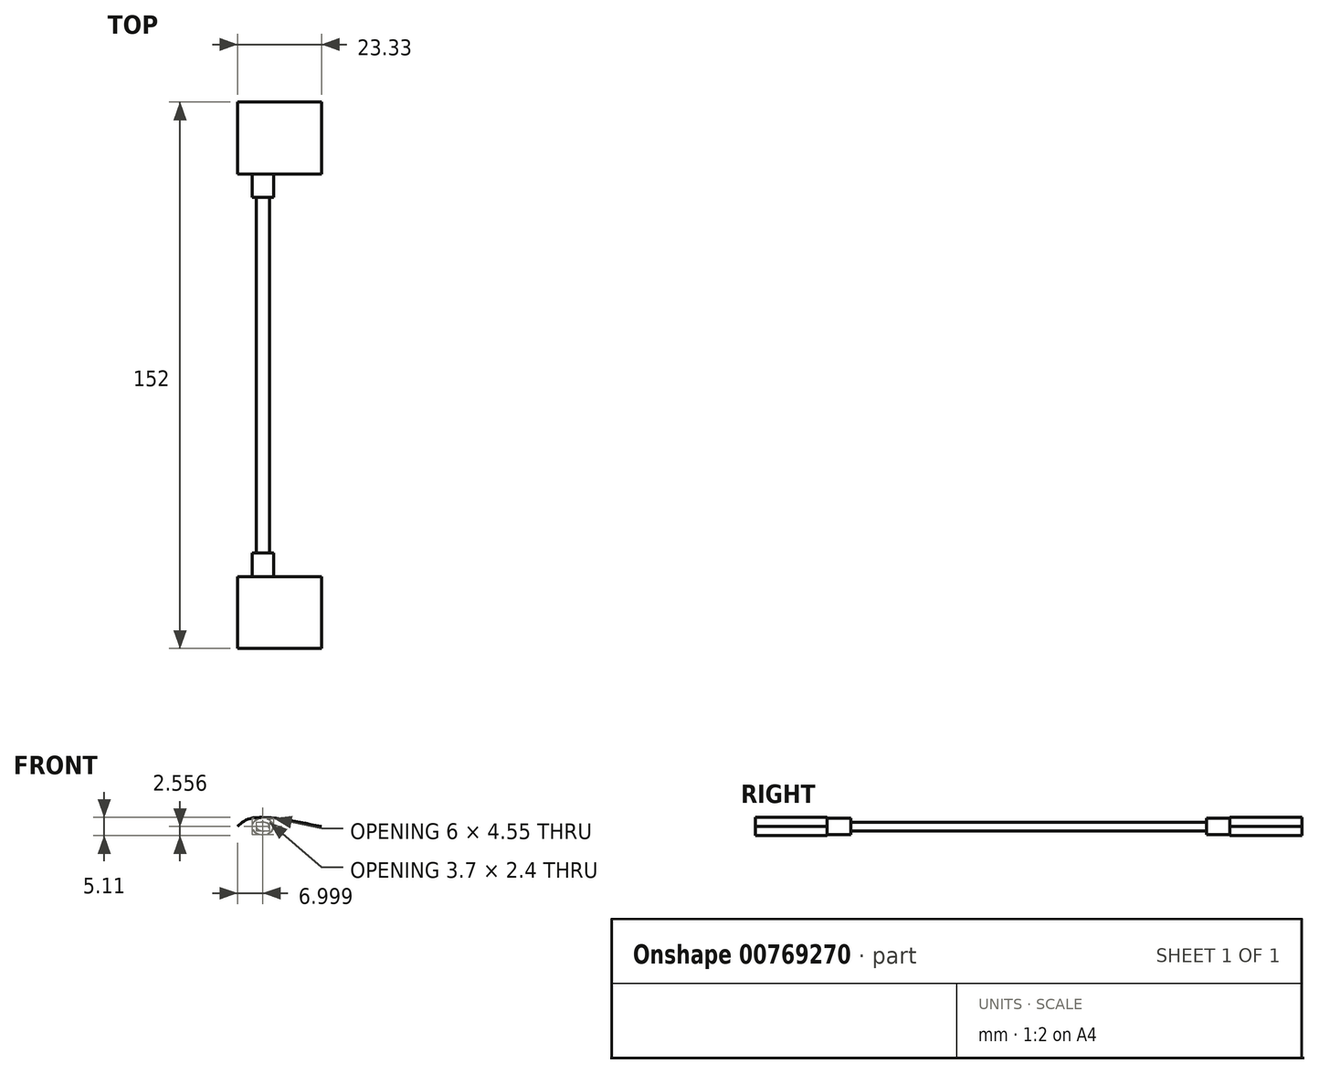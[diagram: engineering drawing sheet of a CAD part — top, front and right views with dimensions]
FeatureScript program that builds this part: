
annotation { "Feature Type Name" : "Feature", "Feature Type Description" : "" }
export const myFeature = defineFeature(function(context is Context, id is Id, definition is map)
    precondition{}
    {
        {
            var Q0;
            Q0=qCreatedBy(makeId("Front.planeOp"),FACE);
            var sketch = newSketch(context, id + "F0", { "sketchPlane" : qUnion([Q0])});
            skLineSegment(sketch, "E0", {"start": v(-22.8, 41.43) * mm, "end": v(4.53, 41.43) * mm, "construction": true});
            skPoint(sketch, "E0.startSnap0", {"position": v(-20.96, 41.43) * mm});
            skFitSpline(sketch, "E1", {"points": [v(-20.96, 41.43) * mm, v(-17.01, 43.75) * mm, v(2.37, 41.43) * mm], "startDerivative": vector(9.37, 8.85) * mm, "endDerivative": vector(34.4, -7.01) * mm});
            skLineSegment(sketch, "E2", {"start": v(-17.01, 45.36) * mm, "end": v(-17.01, 37.43) * mm, "construction": true});
            skFitSpline(sketch, "E3", {"points": [v(-20.96, 41.43) * mm, v(-17.01, 39.1) * mm, v(2.37, 41.43) * mm], "startDerivative": vector(9.37, -8.85) * mm, "endDerivative": vector(34.4, 7.01) * mm});
            skSolve(sketch);
        }
        {
            var Q0;
            Q0 = qSketchRegion(id + "F0", true);
            extrude(context, id + "F1", {"entities" : qUnion([Q0]), "depth" : 20 * mm, "offsetDistance" : 25 * mm});
        }
        {
            var Q0;
            Q0=makeQuery(id+"F1.opExtrude","CAP_FACE",FACE,{"disambiguationData":[OSD([sQuery(id+"F0.wireOp",EDGE,"E1"),sQuery(id+"F0.wireOp",EDGE,"E3")])],"isStart":false});
            var sketch = newSketch(context, id + "F2", { "sketchPlane" : qUnion([Q0])});
            skLineSegment(sketch, "E4", {"start": v(-20.96, 41.43) * mm, "end": v(2.37, 41.43) * mm, "construction": true});
            skEllipse(sketch, "E5", {"center": v(-13.96, 41.43) * mm, "majorRadius": 3 * mm, "minorRadius": 2.27 * mm, "majorAxis": v(1, 0)});
            skSolve(sketch);
        }
        {
            var Q0;
            Q0 = qSketchRegion(id + "F2", true);
            extrude(context, id + "F3", {"entities" : qUnion([Q0]), "operationType" : NewBodyOperationType.ADD, "depth" : 6.5 * mm, "offsetDistance" : 25 * mm});
        }
        {
            var Q0;
            Q0=makeQuery(id+"F3.opExtrude","CAP_FACE",FACE,{"disambiguationData":[OSD([sQuery(id+"F2.wireOp",EDGE,"E5")])],"isStart":false});
            var sketch = newSketch(context, id + "F4", { "sketchPlane" : qUnion([Q0])});
            skEllipse(sketch, "E6", {"center": v(-13.96, 41.43) * mm, "majorRadius": 1.85 * mm, "minorRadius": 1.2 * mm, "majorAxis": v(1, 0)});
            skSolve(sketch);
        }
        {
            var Q0;
            Q0=makeQuery(id+"F4.imprint","IMPRINT",FACE,{"disambiguationData":[TD([[makeQuery(id+"F4.imprint","IMPRINT",EDGE,{"derivedFrom":sQuery(id+"F4.wireOp",EDGE,"E6")}),1.0]])]});
            extrude(context, id + "F5", {"entities" : qUnion([Q0]), "operationType" : NewBodyOperationType.ADD, "depth" : (99 / 2) * mm, "offsetDistance" : 25 * mm});
        }
        {
            var Q0;
            Q0=makeQuery(id+"F1.opExtrude","SWEPT_BODY",BODY,{"disambiguationData":[OSD([sQuery(id+"F0.wireOp",EDGE,"E1"),sQuery(id+"F0.wireOp",EDGE,"E3")])]});
            var Q1;
            Q1=makeQuery(id+"F5.opExtrude","CAP_FACE",FACE,{"disambiguationData":[OSD([sQuery(id+"F4.wireOp",EDGE,"E6")])],"isStart":false});
            mirror(context, id + "F6", {"operationType" : NewBodyOperationType.ADD, "entities" : qUnion([Q0]), "mirrorPlane" : qUnion([Q1])});
        }
    });
